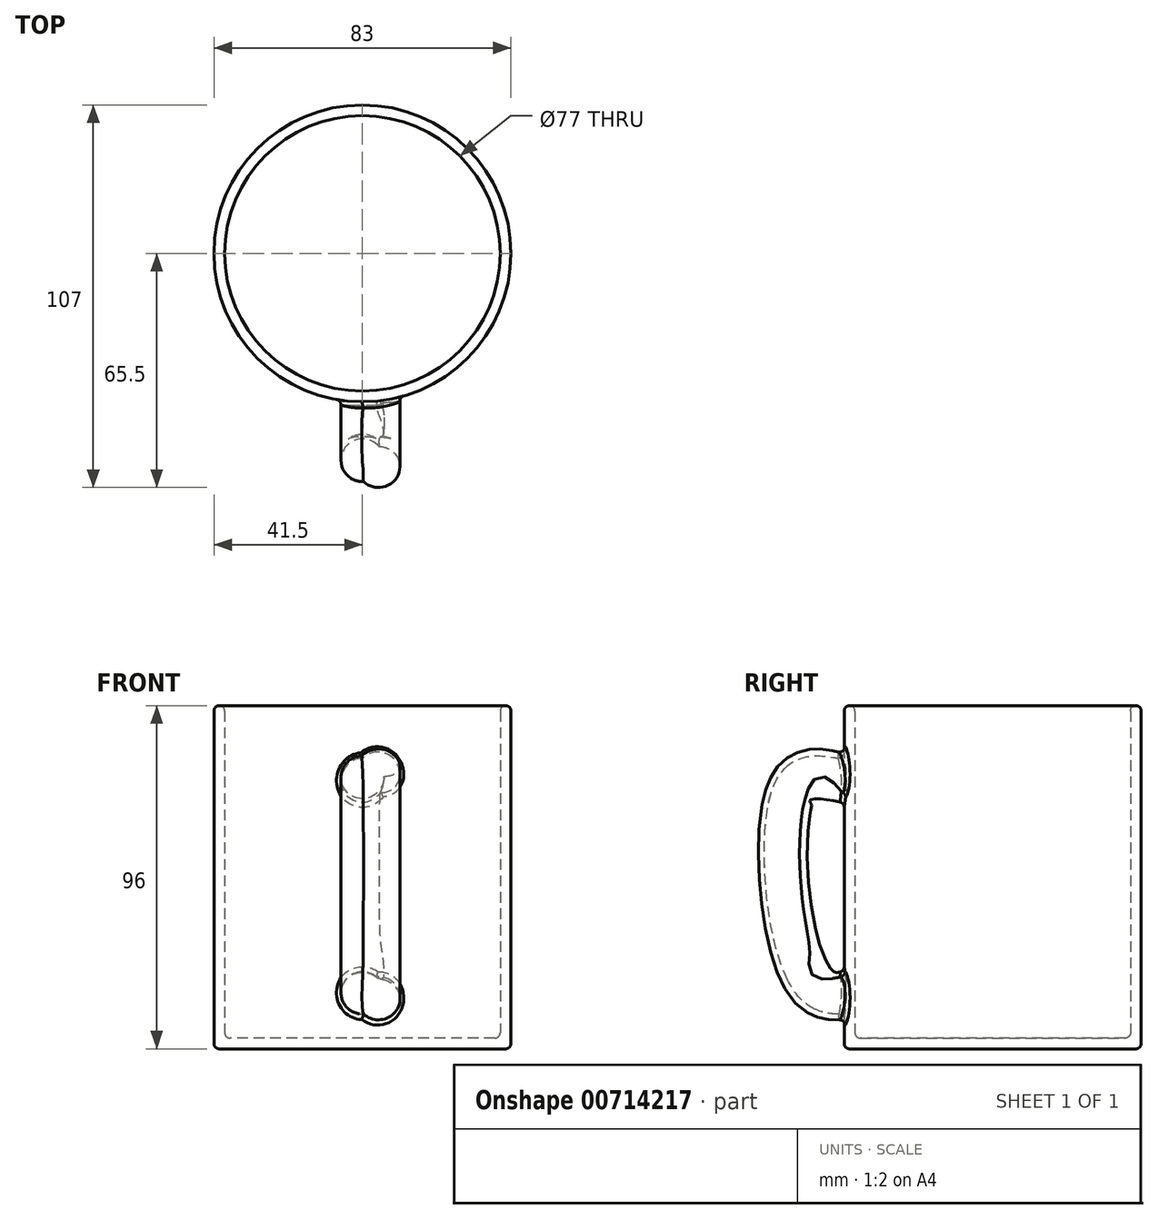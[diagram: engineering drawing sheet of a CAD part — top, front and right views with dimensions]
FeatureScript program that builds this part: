
annotation { "Feature Type Name" : "Feature", "Feature Type Description" : "" }
export const myFeature = defineFeature(function(context is Context, id is Id, definition is map)
    precondition{}
    {
        {
            var Q0;
            Q0=qCreatedBy(makeId("Top.planeOp"),FACE);
            var sketch = newSketch(context, id + "F0", { "sketchPlane" : qUnion([Q0])});
            skCircle(sketch, "E0", {"center": v(0, 0) * mm, "radius": 41.5 * mm});
            skSolve(sketch);
        }
        {
            var Q0;
            Q0=makeQuery(id+"F0.imprint","IMPRINT",FACE,{"disambiguationData":[TD([[makeQuery(id+"F0.imprint","IMPRINT",EDGE,{"derivedFrom":sQuery(id+"F0.wireOp",EDGE,"E0")}),1.0]])]});
            extrude(context, id + "F1", {"entities" : qUnion([Q0]), "depth" : 96 * mm, "offsetDistance" : 25 * mm});
        }
        {
            var Q0;
            Q0=qCreatedBy(makeId("Right.planeOp"),FACE);
            var sketch = newSketch(context, id + "F2", { "sketchPlane" : qUnion([Q0])});
            skFitSpline(sketch, "E1", {"points": [v(-36.37, 74) * mm, v(-45.87, 75.93) * mm, v(-55.46, 72.1) * mm, v(-50.16, 18.74) * mm, v(-33.21, 15.9) * mm], "startDerivative": vector(-52.53, 12.86) * mm, "endDerivative": vector(83.7, -6.09) * mm});
            skSolve(sketch);
        }
        {
            var Q0;
            Q0=qCreatedBy(makeId("Front.planeOp"),FACE);
            cPlane(context, id + "F3", {"entities" : qUnion([Q0]), "cplaneType" : CPlaneType.OFFSET, "offset" : 31 * mm, "width" : 150 * mm, "height" : 150 * mm});
        }
        {
            var Q0;
            Q0=qCreatedBy(id+"F3.planeOp",FACE);
            var sketch = newSketch(context, id + "F4", { "sketchPlane" : qUnion([Q0])});
            skCircle(sketch, "E2", {"center": v(4.48, 74.2) * mm, "radius": 6 * mm});
            skCircle(sketch, "E3", {"center": v(0, 16.06) * mm, "radius": 6 * mm});
            skSolve(sketch);
        }
        {
            var Q0;
            Q0 = qSketchRegion(id + "F4", true);
            var Q1;
            Q1 = qConstructionFilter(qBodyType(qCreatedBy(id + "F2" ,EDGE), BodyType.WIRE), ConstructionObject.NO);
            sweep(context, id + "F5", {"operationType" : NewBodyOperationType.ADD, "profiles" : qUnion([Q0]), "path" : qUnion([Q1])});
        }
        {
            var Q0;
            Q0=makeQuery(id+"F1.opExtrude","CAP_FACE",FACE,{"disambiguationData":[OSD([sQuery(id+"F0.wireOp",EDGE,"E0")])],"isStart":false});
            shell(context, id + "F6", {"entities" : qUnion([Q0]), "thickness" : 3 * mm});
        }
        {
            var Q0;
            {var subQ0=sQuery(id+"F0.wireOp",EDGE,"E0");Q0=makeQuery(id+"F6.opShell","OFFSET_EDGE",EDGE,{"disambiguationData":[OSD([subQ0]),TDD([makeQuery(id+"F1.opExtrude","CAP_EDGE",EDGE,{"disambiguationData":[OSD([subQ0])],"isStart":false})])]});}
            var Q1;
            Q1=makeQuery(id+"F1.opExtrude","CAP_EDGE",EDGE,{"disambiguationData":[OSD([sQuery(id+"F0.wireOp",EDGE,"E0")])],"isStart":false});
            var Q2;
            Q2=makeQuery(id+"F5.boolean.opBoolean","INTERSECT",EDGE,{"disambiguationData":[OD(1.0)],"derivedFrom":[makeQuery(id+"F1.opExtrude","SWEPT_FACE",FACE,{"disambiguationData":[OSD([sQuery(id+"F0.wireOp",EDGE,"E0")])]}),makeQuery(id+"F5.opSweep","SWEPT_FACE",FACE,{"disambiguationData":[OSD([sQuery(id+"F2.wireOp",EDGE,"E1"),sQuery(id+"F4.wireOp",EDGE,"E3")])]})]});
            var Q3;
            Q3=makeQuery(id+"F5.boolean.opBoolean","INTERSECT",EDGE,{"disambiguationData":[OD(1.0)],"derivedFrom":[makeQuery(id+"F1.opExtrude","SWEPT_FACE",FACE,{"disambiguationData":[OSD([sQuery(id+"F0.wireOp",EDGE,"E0")])]}),makeQuery(id+"F5.opSweep","SWEPT_FACE",FACE,{"disambiguationData":[OSD([sQuery(id+"F2.wireOp",EDGE,"E1"),sQuery(id+"F4.wireOp",EDGE,"E2")])]})]});
            var Q4;
            Q4=makeQuery(id+"F1.opExtrude","CAP_FACE",FACE,{"disambiguationData":[OSD([sQuery(id+"F0.wireOp",EDGE,"E0")])],"isStart":true});
            var Q5;
            Q5=makeQuery(id+"F5.boolean.opBoolean","INTERSECT",EDGE,{"disambiguationData":[OD(0.0)],"derivedFrom":[makeQuery(id+"F1.opExtrude","SWEPT_FACE",FACE,{"disambiguationData":[OSD([sQuery(id+"F0.wireOp",EDGE,"E0")])]}),makeQuery(id+"F5.opSweep","SWEPT_FACE",FACE,{"disambiguationData":[OSD([sQuery(id+"F2.wireOp",EDGE,"E1"),sQuery(id+"F4.wireOp",EDGE,"E2")])]})]});
            var Q6;
            Q6=makeQuery(id+"F5.boolean.opBoolean","INTERSECT",EDGE,{"disambiguationData":[OD(0.0)],"derivedFrom":[makeQuery(id+"F1.opExtrude","SWEPT_FACE",FACE,{"disambiguationData":[OSD([sQuery(id+"F0.wireOp",EDGE,"E0")])]}),makeQuery(id+"F5.opSweep","SWEPT_FACE",FACE,{"disambiguationData":[OSD([sQuery(id+"F2.wireOp",EDGE,"E1"),sQuery(id+"F4.wireOp",EDGE,"E3")])]})]});
            var Q7;
            {var subQ0=sQuery(id+"F0.wireOp",EDGE,"E0");Q7=makeQuery(id+"F6.opShell","OFFSET_FACE",FACE,{"disambiguationData":[OSD([subQ0]),TDD([makeQuery(id+"F1.opExtrude","CAP_FACE",FACE,{"disambiguationData":[OSD([subQ0])],"isStart":true})])]});}
            fillet(context, id + "F7", {"entities" : qUnion([Q0, Q1, Q2, Q3, Q4, Q5, Q6, Q7]), "radius" : 1.5 * mm, "tangentPropagation" : true, "allowEdgeOverflow" : false});
        }
    });
